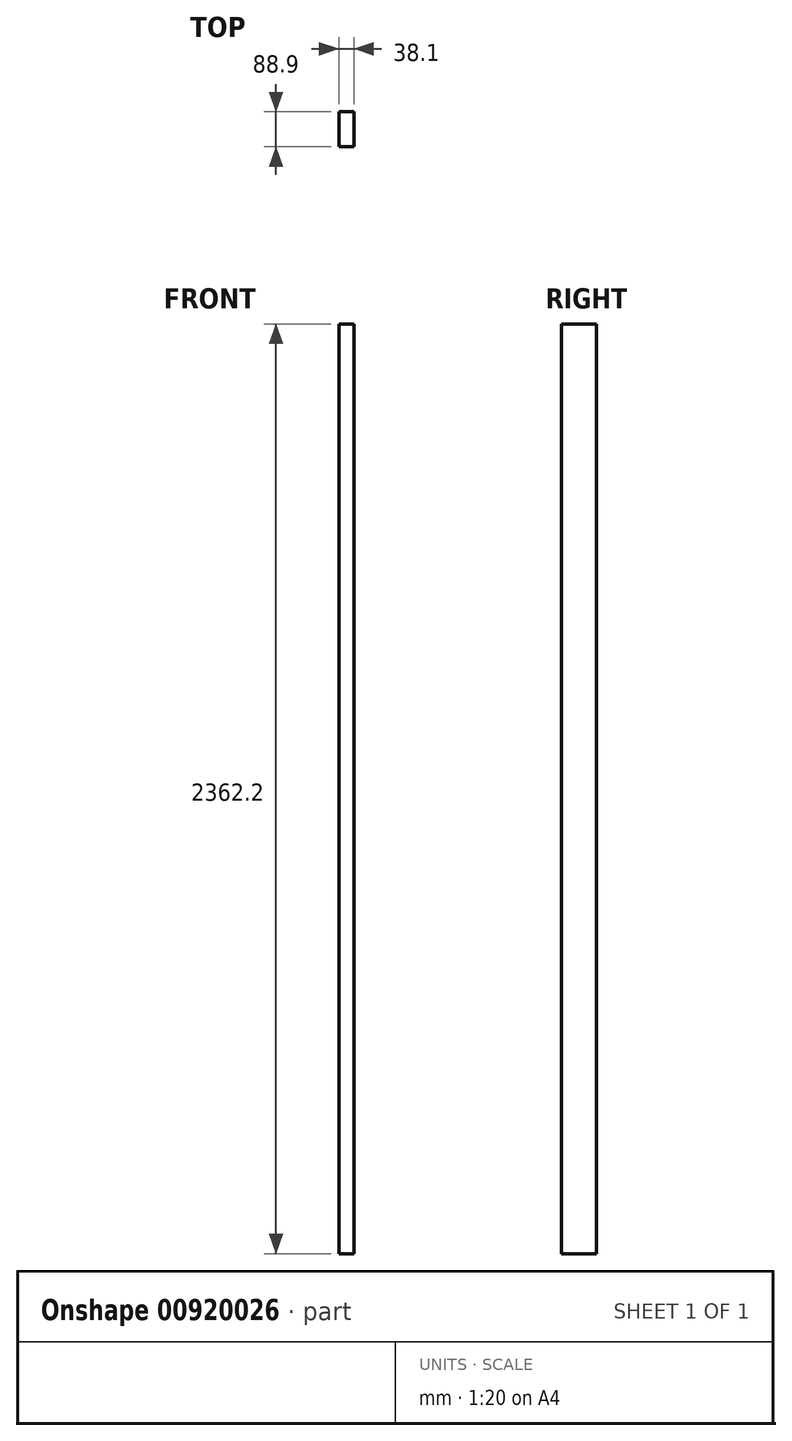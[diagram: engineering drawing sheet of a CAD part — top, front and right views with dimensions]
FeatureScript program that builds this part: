
annotation { "Feature Type Name" : "Feature", "Feature Type Description" : "" }
export const myFeature = defineFeature(function(context is Context, id is Id, definition is map)
    precondition{}
    {
        {
            var Q0;
            Q0=qCreatedBy(makeId("Top.planeOp"),FACE);
            var sketch = newSketch(context, id + "F0", { "sketchPlane" : qUnion([Q0])});
            skLineSegment(sketch, "E0.bottom", {"start": v(19.05, -44.45) * mm, "end": v(-19.05, -44.45) * mm});
            skLineSegment(sketch, "E0.top", {"start": v(19.05, 44.45) * mm, "end": v(-19.05, 44.45) * mm});
            skLineSegment(sketch, "E0.left", {"start": v(19.05, -44.45) * mm, "end": v(19.05, 44.45) * mm});
            skLineSegment(sketch, "E0.right", {"start": v(-19.05, -44.45) * mm, "end": v(-19.05, 44.45) * mm});
            skPoint(sketch, "E0.middle", {"position": v(0, 0) * mm});
            skSolve(sketch);
        }
        {
            var Q0;
            Q0 = qSketchRegion(id + "F0", true);
            extrude(context, id + "F1", {"entities" : qUnion([Q0]), "depth" : 2362.2 * mm, "offsetDistance" : 25.4 * mm});
        }
    });
